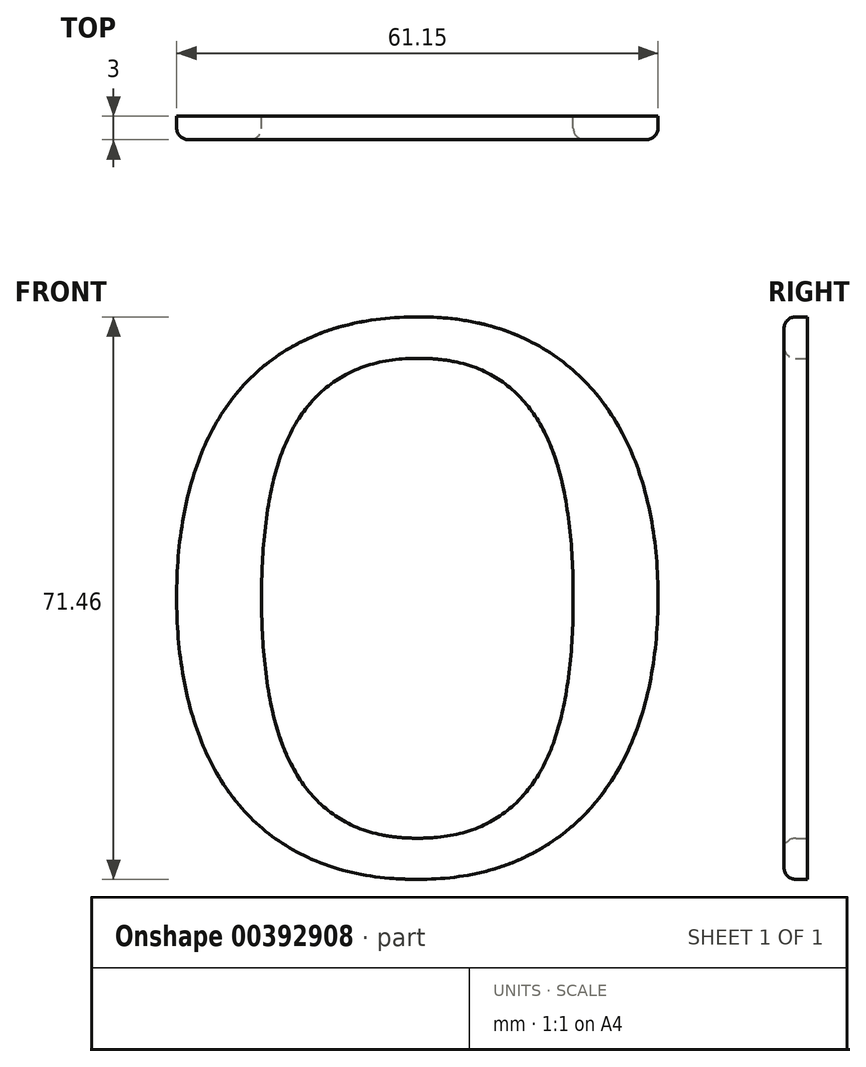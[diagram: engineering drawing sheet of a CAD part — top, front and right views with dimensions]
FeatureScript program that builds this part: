
annotation { "Feature Type Name" : "Feature", "Feature Type Description" : "" }
export const myFeature = defineFeature(function(context is Context, id is Id, definition is map)
    precondition{}
    {
        {
            var Q0;
            Q0=qCreatedBy(makeId("Front.planeOp"),FACE);
            var sketch = newSketch(context, id + "F0", { "sketchPlane" : qUnion([Q0])});
            skText(sketch, "E0", { "text": "O", "fontName": "NotoSerif-Regular.ttf"});
            const initialGuessF0  = {"E0": [0.00362, 0, 1, 0, 0.07]};
            skSetInitialGuess(sketch, initialGuessF0);
            skSolve(sketch);
        }
        {
            var Q0;
            Q0 = qSketchRegion(id + "F0", true);
            extrude(context, id + "F1", {"entities" : qUnion([Q0]), "depth" : 3 * mm});
        }
        {
            var Q0;
            Q0=makeQuery(id+"F1.opExtrude","CAP_FACE",FACE,{"disambiguationData":[OSD([sQuery(id+"F0.wireOp",EDGE,"E0.sketch_text.stroke-0"),sQuery(id+"F0.wireOp",EDGE,"E0.sketch_text.stroke-1"),sQuery(id+"F0.wireOp",EDGE,"E0.sketch_text.stroke-2"),sQuery(id+"F0.wireOp",EDGE,"E0.sketch_text.stroke-3"),sQuery(id+"F0.wireOp",EDGE,"E0.sketch_text.stroke-4"),sQuery(id+"F0.wireOp",EDGE,"E0.sketch_text.stroke-5"),sQuery(id+"F0.wireOp",EDGE,"E0.sketch_text.stroke-6"),sQuery(id+"F0.wireOp",EDGE,"E0.sketch_text.stroke-7"),sQuery(id+"F0.wireOp",EDGE,"E0.sketch_text.stroke-8"),sQuery(id+"F0.wireOp",EDGE,"E0.sketch_text.stroke-9"),sQuery(id+"F0.wireOp",EDGE,"E0.sketch_text.stroke-10"),sQuery(id+"F0.wireOp",EDGE,"E0.sketch_text.stroke-11"),sQuery(id+"F0.wireOp",EDGE,"E0.sketch_text.stroke-12"),sQuery(id+"F0.wireOp",EDGE,"E0.sketch_text.stroke-13"),sQuery(id+"F0.wireOp",EDGE,"E0.sketch_text.stroke-14"),sQuery(id+"F0.wireOp",EDGE,"E0.sketch_text.stroke-15"),sQuery(id+"F0.wireOp",EDGE,"E0.sketch_text.stroke-16"),sQuery(id+"F0.wireOp",EDGE,"E0.sketch_text.stroke-17"),sQuery(id+"F0.wireOp",EDGE,"E0.sketch_text.stroke-18"),sQuery(id+"F0.wireOp",EDGE,"E0.sketch_text.stroke-19"),sQuery(id+"F0.wireOp",EDGE,"E0.sketch_text.stroke-20"),sQuery(id+"F0.wireOp",EDGE,"E0.sketch_text.stroke-21"),sQuery(id+"F0.wireOp",EDGE,"E0.sketch_text.stroke-22"),sQuery(id+"F0.wireOp",EDGE,"E0.sketch_text.stroke-23"),sQuery(id+"F0.wireOp",EDGE,"E0.sketch_text.stroke-24"),sQuery(id+"F0.wireOp",EDGE,"E0.sketch_text.stroke-25"),sQuery(id+"F0.wireOp",EDGE,"E0.sketch_text.stroke-26"),sQuery(id+"F0.wireOp",EDGE,"E0.sketch_text.stroke-27"),sQuery(id+"F0.wireOp",EDGE,"E0.sketch_text.stroke-28"),sQuery(id+"F0.wireOp",EDGE,"E0.sketch_text.stroke-29"),sQuery(id+"F0.wireOp",EDGE,"E0.sketch_text.stroke-30"),sQuery(id+"F0.wireOp",EDGE,"E0.sketch_text.stroke-31")])],"isStart":false});
            fillet(context, id + "F2", {"entities" : qUnion([Q0]), "radius" : 1.5 * mm, "tangentPropagation" : true, "allowEdgeOverflow" : false});
        }
    });
